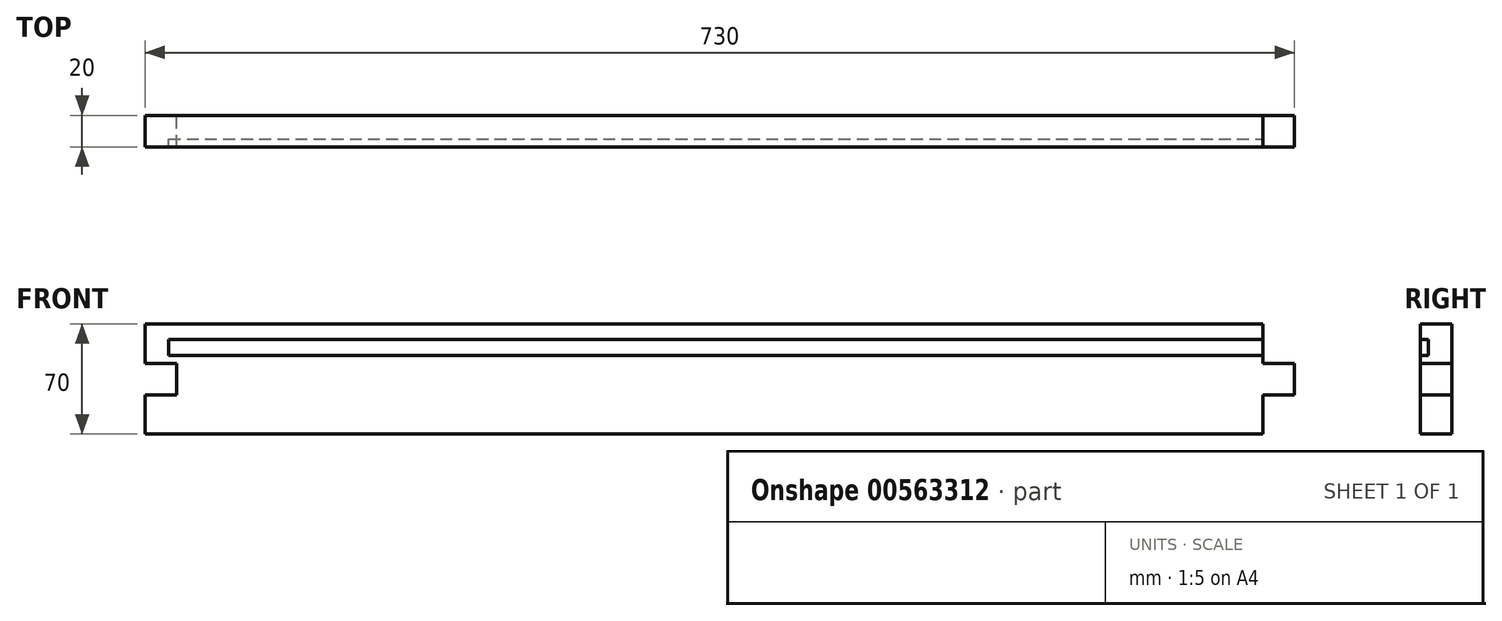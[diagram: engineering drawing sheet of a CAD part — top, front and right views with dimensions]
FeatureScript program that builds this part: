
annotation { "Feature Type Name" : "Feature", "Feature Type Description" : "" }
export const myFeature = defineFeature(function(context is Context, id is Id, definition is map)
    precondition{}
    {
        {
            var Q0;
            Q0=qCreatedBy(makeId("Top.planeOp"),FACE);
            var sketch = newSketch(context, id + "F0", { "sketchPlane" : qUnion([Q0])});
            skLineSegment(sketch, "E0.bottom", {"start": v(-404.74, -7.95) * mm, "end": v(325.26, -7.95) * mm});
            skLineSegment(sketch, "E0.top", {"start": v(-404.74, -27.95) * mm, "end": v(325.26, -27.95) * mm});
            skLineSegment(sketch, "E0.left", {"start": v(-404.74, -7.95) * mm, "end": v(-404.74, -27.95) * mm});
            skLineSegment(sketch, "E0.right", {"start": v(325.26, -7.95) * mm, "end": v(325.26, -27.95) * mm});
            skSolve(sketch);
        }
        {
            var Q0;
            Q0 = qSketchRegion(id + "F0", true);
            extrude(context, id + "F1", {"entities" : qUnion([Q0]), "depth" : 70 * mm, "offsetDistance" : 25 * mm});
        }
        {
            var Q0;
            Q0=makeQuery(id+"F1.opExtrude","SWEPT_FACE",FACE,{"disambiguationData":[OSD([sQuery(id+"F0.wireOp",EDGE,"E0.right")])]});
            var sketch = newSketch(context, id + "F2", { "sketchPlane" : qUnion([Q0])});
            skLineSegment(sketch, "E1.bottom", {"start": v(-27.95, 60) * mm, "end": v(-22.95, 60) * mm});
            skLineSegment(sketch, "E1.top", {"start": v(-27.95, 50) * mm, "end": v(-22.95, 50) * mm});
            skLineSegment(sketch, "E1.left", {"start": v(-27.95, 60) * mm, "end": v(-27.95, 50) * mm});
            skLineSegment(sketch, "E1.right", {"start": v(-22.95, 60) * mm, "end": v(-22.95, 50) * mm});
            skSolve(sketch);
        }
        {
            var Q0;
            Q0 = qSketchRegion(id + "F2", true);
            extrude(context, id + "F3", {"entities" : qUnion([Q0]), "operationType" : NewBodyOperationType.REMOVE, "oppositeDirection" : true, "depth" : 715 * mm, "offsetDistance" : 25 * mm, "hasSecondDirection" : true, "secondDirectionOppositeDirection" : true, "secondDirectionDepth" : 15 * mm});
        }
        {
            var Q0;
            Q0=makeQuery(id+"F1.opExtrude","SWEPT_FACE",FACE,{"disambiguationData":[OSD([sQuery(id+"F0.wireOp",EDGE,"E0.bottom")])]});
            var sketch = newSketch(context, id + "F4", { "sketchPlane" : qUnion([Q0])});
            skLineSegment(sketch, "E2.bottom", {"start": v(-325.26, 70) * mm, "end": v(-305.26, 70) * mm});
            skLineSegment(sketch, "E2.top", {"start": v(-325.26, 45) * mm, "end": v(-305.26, 45) * mm});
            skLineSegment(sketch, "E2.left", {"start": v(-325.26, 70) * mm, "end": v(-325.26, 45) * mm});
            skLineSegment(sketch, "E2.right", {"start": v(-305.26, 70) * mm, "end": v(-305.26, 45) * mm});
            skLineSegment(sketch, "E3.bottom", {"start": v(-325.26, 0) * mm, "end": v(-305.26, 0) * mm});
            skLineSegment(sketch, "E3.top", {"start": v(-325.26, 25) * mm, "end": v(-305.26, 25) * mm});
            skLineSegment(sketch, "E3.left", {"start": v(-325.26, 0) * mm, "end": v(-325.26, 25) * mm});
            skLineSegment(sketch, "E3.right", {"start": v(-305.26, 0) * mm, "end": v(-305.26, 25) * mm});
            skLineSegment(sketch, "E4.bottom", {"start": v(404.74, 45) * mm, "end": v(384.74, 45) * mm});
            skLineSegment(sketch, "E4.top", {"start": v(404.74, 25) * mm, "end": v(384.74, 25) * mm});
            skLineSegment(sketch, "E4.left", {"start": v(404.74, 45) * mm, "end": v(404.74, 25) * mm});
            skLineSegment(sketch, "E4.right", {"start": v(384.74, 45) * mm, "end": v(384.74, 25) * mm});
            skSolve(sketch);
        }
        {
            var Q0;
            Q0=makeQuery(id+"F4.imprint","IMPRINT",FACE,{"disambiguationData":[TD([[makeQuery(id+"F4.imprint","IMPRINT",EDGE,{"derivedFrom":sQuery(id+"F4.wireOp",EDGE,"E2.bottom")}),1.0]])]});
            var Q1;
            Q1=makeQuery(id+"F4.imprint","IMPRINT",FACE,{"disambiguationData":[TD([[makeQuery(id+"F4.imprint","IMPRINT",EDGE,{"derivedFrom":sQuery(id+"F4.wireOp",EDGE,"E3.bottom")}),-1.0]])]});
            var Q2;
            Q2=makeQuery(id+"F4.imprint","IMPRINT",FACE,{"disambiguationData":[TD([[makeQuery(id+"F4.imprint","IMPRINT",EDGE,{"derivedFrom":sQuery(id+"F4.wireOp",EDGE,"E4.bottom")}),1.0]])]});
            extrude(context, id + "F5", {"entities" : qUnion([Q0, Q1, Q2]), "operationType" : NewBodyOperationType.REMOVE, "endBound" : BoundingType.THROUGH_ALL, "oppositeDirection" : true, "depth" : 25 * mm, "offsetDistance" : 25 * mm});
        }
    });
